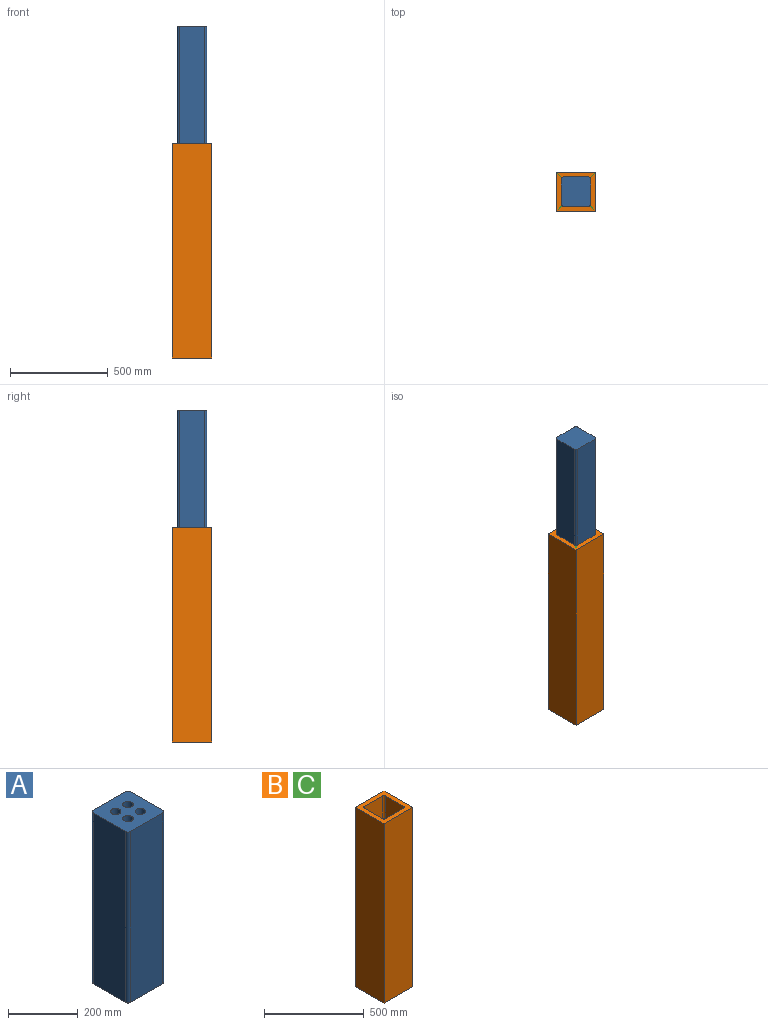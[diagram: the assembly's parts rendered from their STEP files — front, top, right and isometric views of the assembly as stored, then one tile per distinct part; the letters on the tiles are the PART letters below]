
ASSEMBLY  parts=3 mates=1
PART A: 18 faces, bbox 150x150x600 mm
  f0: plane 600x130mm, normal (0,1,0), area 78000mm2, adj f4,f5,f6,f9
  f1: plane 600x130mm, normal (-1,0,0), area 78000mm2, adj f4,f5,f6,f7
  f2: plane 600x130mm, normal (0,-1,0), area 78000mm2, adj f4,f5,f7,f8
  f3: plane 600x130mm, normal (1,0,0), area 78000mm2, adj f4,f5,f8,f9
  f4: plane 150x150mm, normal (0,0,1), area 19586.7mm2, adj f0,f1,f2,f3,f6,f7,f8,f9
  f5: plane 150x150mm, normal (0,0,-1), area 22414.2mm2, adj f0,f1,f2,f3,f6,f7,f8,f9
  f6: cylinder r=10mm len=600mm, axis (0,0,-1), area 9424.8mm2, adj f0,f1,f4,f5
  f7: cylinder r=10mm len=600mm, axis (0,0,1), area 9424.8mm2, adj f1,f2,f4,f5
  f8: cylinder r=10mm len=600mm, axis (0,0,-1), area 9424.8mm2, adj f2,f3,f4,f5
  f9: cylinder r=10mm len=600mm, axis (0,0,1), area 9424.8mm2, adj f0,f3,f4,f5
  f10: cylinder r=15mm len=50mm, axis (0,0,1), area 4712.4mm2, adj f4,f11
  f11: plane 30x30mm, normal (0,0,1), area 706.9mm2, adj f10
  f12: cylinder r=15mm len=50mm, axis (0,0,1), area 4712.4mm2, adj f4,f13
  f13: plane 30x30mm, normal (0,0,1), area 706.9mm2, adj f12
  f14: cylinder r=15mm len=50mm, axis (0,0,1), area 4712.4mm2, adj f4,f15
  f15: plane 30x30mm, normal (0,0,1), area 706.9mm2, adj f14
  f16: cylinder r=15mm len=50mm, axis (0,0,1), area 4712.4mm2, adj f4,f17
  f17: plane 30x30mm, normal (0,0,1), area 706.9mm2, adj f16
PART B: 15 faces, bbox 200x200x1100 mm
  f0: plane 200x200mm, normal (0,0,1), area 17585.8mm2, adj f1,f3,f4,f5,f6,f7,f8,f9
  f1: plane 1100x200mm, normal (0,-1,0), area 220000mm2, adj f0,f2,f4,f5
  f2: plane 200x200mm, normal (0,0,-1), area 40000mm2, adj f1,f3,f4,f5
  f3: plane 1100x200mm, normal (0,1,0), area 220000mm2, adj f0,f2,f4,f5
  f4: plane 1100x200mm, normal (1,0,0), area 220000mm2, adj f0,f1,f2,f3
  f5: plane 1100x200mm, normal (-1,0,0), area 220000mm2, adj f0,f1,f2,f3
  f6: plane 500x130mm, normal (1,0,0), area 65000mm2, adj f0,f10,f11,f14
  f7: plane 500x130mm, normal (0,1,0), area 65000mm2, adj f0,f10,f11,f12
  f8: plane 500x130mm, normal (-1,0,0), area 65000mm2, adj f0,f10,f12,f13
  f9: plane 500x130mm, normal (0,-1,0), area 65000mm2, adj f0,f10,f13,f14
  f10: plane 150x150mm, normal (0,0,1), area 22414.2mm2, adj f6,f7,f8,f9,f11,f12,f13,f14
  f11: cylinder r=10mm len=500mm, axis (0,0,-1), area 7854mm2, adj f0,f6,f7,f10
  f12: cylinder r=10mm len=500mm, axis (0,0,1), area 7854mm2, adj f0,f7,f8,f10
  f13: cylinder r=10mm len=500mm, axis (0,0,-1), area 7854mm2, adj f0,f8,f9,f10
  f14: cylinder r=10mm len=500mm, axis (0,0,1), area 7854mm2, adj f0,f6,f9,f10
PART C: same geometry as B
PLACE A rot(axis=(0.71,0.71,0),180deg) t=(25,25,1700)mm
PLACE B at identity
PLACE C at identity
MATE slider A.f4 <-> C.f10  axis (0,0,-1) through (100,100,1100)mm
